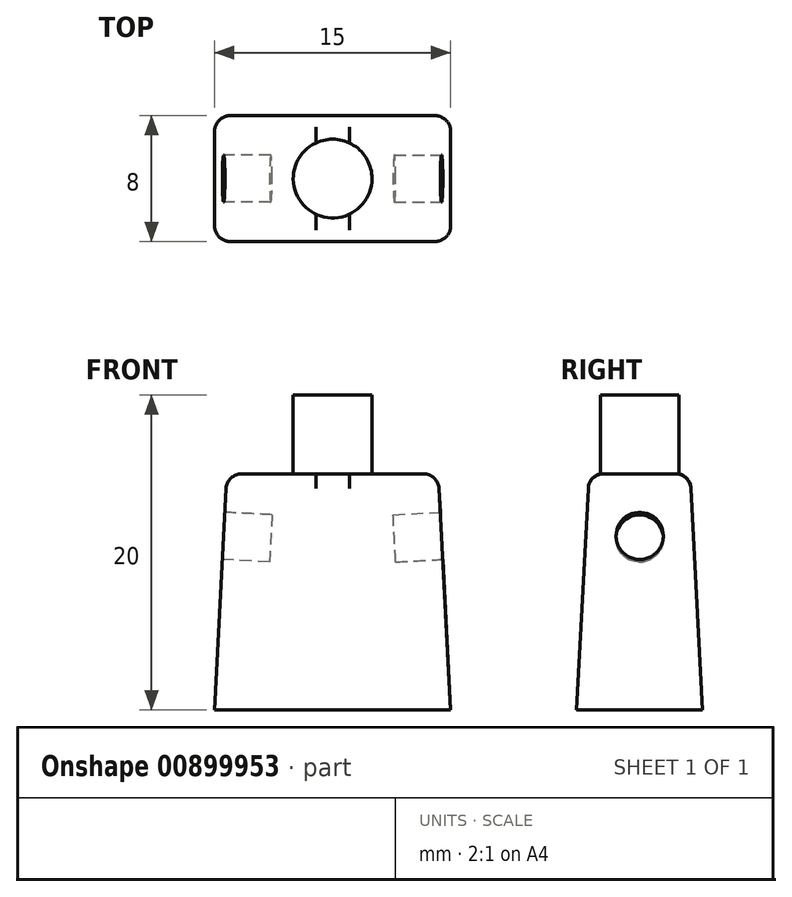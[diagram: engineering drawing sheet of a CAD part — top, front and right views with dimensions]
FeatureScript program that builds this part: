
annotation { "Feature Type Name" : "Feature", "Feature Type Description" : "" }
export const myFeature = defineFeature(function(context is Context, id is Id, definition is map)
    precondition{}
    {
        {
            var Q0;
            Q0=qCreatedBy(makeId("Top.planeOp"),FACE);
            var sketch = newSketch(context, id + "F0", { "sketchPlane" : qUnion([Q0])});
            skLineSegment(sketch, "E0.bottom", {"start": v(7.5, 4) * mm, "end": v(-7.5, 4) * mm});
            skLineSegment(sketch, "E0.top", {"start": v(7.5, -4) * mm, "end": v(-7.5, -4) * mm});
            skLineSegment(sketch, "E0.left", {"start": v(7.5, 4) * mm, "end": v(7.5, -4) * mm});
            skLineSegment(sketch, "E0.right", {"start": v(-7.5, 4) * mm, "end": v(-7.5, -4) * mm});
            skPoint(sketch, "E0.middle", {"position": v(0, 0) * mm});
            skSolve(sketch);
        }
        {
            var Q0;
            Q0 = qSketchRegion(id + "F0", true);
            extrude(context, id + "F1", {"entities" : qUnion([Q0]), "depth" : 15 * mm, "offsetDistance" : 25 * mm, "hasDraft" : true, "draftAngle" : 3 * degree, "draftPullDirection" : true});
        }
        {
            var Q0;
            Q0=makeQuery(id+"F1.opExtrude","CAP_FACE",FACE,{"disambiguationData":[OSD([sQuery(id+"F0.wireOp",EDGE,"E0.bottom"),sQuery(id+"F0.wireOp",EDGE,"E0.top"),sQuery(id+"F0.wireOp",EDGE,"E0.left"),sQuery(id+"F0.wireOp",EDGE,"E0.right")])],"isStart":false});
            var sketch = newSketch(context, id + "F2", { "sketchPlane" : qUnion([Q0])});
            skCircle(sketch, "E1", {"center": v(0, 0) * mm, "radius": 2.5 * mm});
            skSolve(sketch);
        }
        {
            var Q0;
            Q0 = qSketchRegion(id + "F2", true);
            extrude(context, id + "F3", {"entities" : qUnion([Q0]), "operationType" : NewBodyOperationType.ADD, "depth" : 5 * mm, "offsetDistance" : 25 * mm});
        }
        {
            var Q0;
            Q0=makeQuery(id+"F1.opExtrude","SWEPT_EDGE",EDGE,{"disambiguationData":[OSD([sQuery(id+"F0.wireOp",EDGE,"E0.top"),sQuery(id+"F0.wireOp",EDGE,"E0.right")])]});
            var Q1;
            Q1=makeQuery(id+"F1.opExtrude","SWEPT_EDGE",EDGE,{"disambiguationData":[OSD([sQuery(id+"F0.wireOp",EDGE,"E0.top"),sQuery(id+"F0.wireOp",EDGE,"E0.left")])]});
            var Q2;
            Q2=makeQuery(id+"F1.opExtrude","SWEPT_EDGE",EDGE,{"disambiguationData":[OSD([sQuery(id+"F0.wireOp",EDGE,"E0.bottom"),sQuery(id+"F0.wireOp",EDGE,"E0.left")])]});
            var Q3;
            Q3=makeQuery(id+"F1.opExtrude","SWEPT_EDGE",EDGE,{"disambiguationData":[OSD([sQuery(id+"F0.wireOp",EDGE,"E0.bottom"),sQuery(id+"F0.wireOp",EDGE,"E0.right")])]});
            var Q4;
            Q4=makeQuery(id+"F1.opExtrude","CAP_EDGE",EDGE,{"disambiguationData":[OSD([sQuery(id+"F0.wireOp",EDGE,"E0.left")])],"isStart":false});
            var Q5;
            Q5=makeQuery(id+"F1.opExtrude","CAP_EDGE",EDGE,{"disambiguationData":[OSD([sQuery(id+"F0.wireOp",EDGE,"E0.top")])],"isStart":false});
            var Q6;
            Q6=makeQuery(id+"F1.opExtrude","CAP_EDGE",EDGE,{"disambiguationData":[OSD([sQuery(id+"F0.wireOp",EDGE,"E0.right")])],"isStart":false});
            var Q7;
            Q7=makeQuery(id+"F1.opExtrude","CAP_EDGE",EDGE,{"disambiguationData":[OSD([sQuery(id+"F0.wireOp",EDGE,"E0.bottom")])],"isStart":false});
            fillet(context, id + "F4", {"entities" : qUnion([Q0, Q1, Q2, Q3, Q4, Q5, Q6, Q7]), "radius" : 1 * mm, "tangentPropagation" : true, "allowEdgeOverflow" : false});
        }
        {
            var Q0;
            Q0=makeQuery(id+"F1.opExtrude","SWEPT_FACE",FACE,{"disambiguationData":[OSD([sQuery(id+"F0.wireOp",EDGE,"E0.left")])]});
            var sketch = newSketch(context, id + "F5", { "sketchPlane" : qUnion([Q0])});
            skCircle(sketch, "E2", {"center": v(0, 10.68) * mm, "radius": 1.5 * mm});
            skSolve(sketch);
        }
        {
            var Q0;
            Q0=makeQuery(id+"F5.imprint","IMPRINT",FACE,{"disambiguationData":[TD([[makeQuery(id+"F5.imprint","IMPRINT",EDGE,{"derivedFrom":sQuery(id+"F5.wireOp",EDGE,"E2")}),1.0]])]});
            extrude(context, id + "F6", {"entities" : qUnion([Q0]), "operationType" : NewBodyOperationType.REMOVE, "oppositeDirection" : true, "depth" : 3 * mm, "offsetDistance" : 25 * mm});
        }
        {
            var Q0;
            Q0=makeQuery(id+"F1.opExtrude","SWEPT_FACE",FACE,{"disambiguationData":[OSD([sQuery(id+"F0.wireOp",EDGE,"E0.right")])]});
            var sketch = newSketch(context, id + "F7", { "sketchPlane" : qUnion([Q0])});
            skCircle(sketch, "E3", {"center": v(0, 10.68) * mm, "radius": 1.5 * mm});
            skSolve(sketch);
        }
        {
            var Q0;
            Q0=makeQuery(id+"F7.imprint","IMPRINT",FACE,{"disambiguationData":[TD([[makeQuery(id+"F7.imprint","IMPRINT",EDGE,{"derivedFrom":sQuery(id+"F7.wireOp",EDGE,"E3")}),1.0]])]});
            extrude(context, id + "F8", {"entities" : qUnion([Q0]), "operationType" : NewBodyOperationType.REMOVE, "oppositeDirection" : true, "depth" : 3 * mm, "offsetDistance" : 25 * mm});
        }
    });
